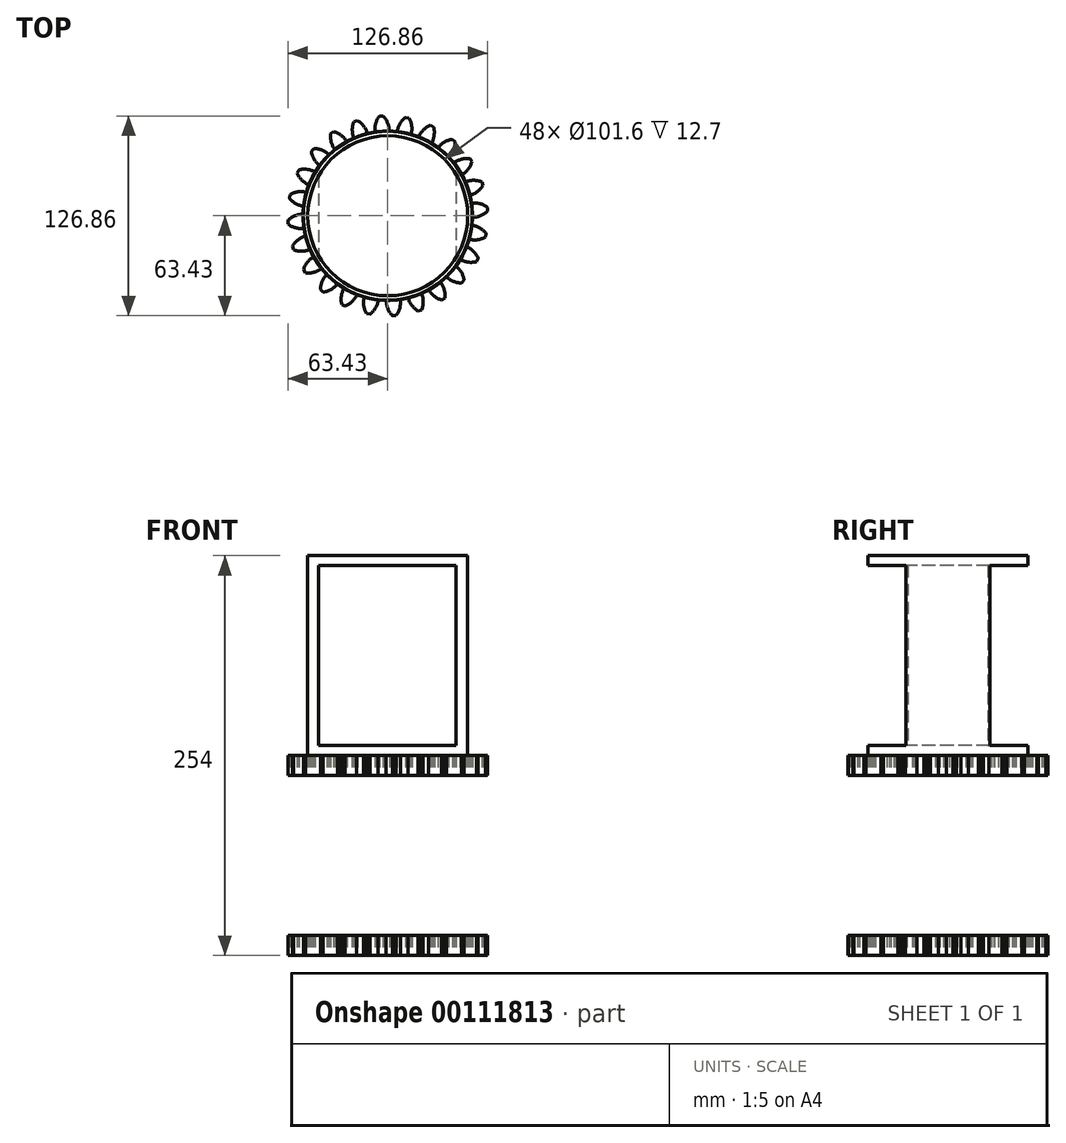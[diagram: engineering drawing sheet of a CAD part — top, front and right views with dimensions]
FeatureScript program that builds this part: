
annotation { "Feature Type Name" : "Feature", "Feature Type Description" : "" }
export const myFeature = defineFeature(function(context is Context, id is Id, definition is map)
    precondition{}
    {
        {
            var Q0;
            Q0=qCreatedBy(makeId("Top.planeOp"),FACE);
            var sketch = newSketch(context, id + "F0", { "sketchPlane" : qUnion([Q0])});
            skCircle(sketch, "E0", {"center": v(0, 0) * mm, "radius": 53.72 * mm});
            skCircle(sketch, "E1", {"center": v(0, 0) * mm, "radius": 58.67 * mm, "construction": true});
            skCircle(sketch, "E2", {"center": v(0, 0) * mm, "radius": 63.5 * mm, "construction": true});
            skLineSegment(sketch, "E3", {"start": v(0, 0) * mm, "end": v(0, 120.75) * mm, "construction": true});
            skLineSegment(sketch, "E4", {"start": v(0, 0) * mm, "end": v(-6.04, 92.19) * mm, "construction": true});
            skLineSegment(sketch, "E5", {"start": v(0, 58.67) * mm, "end": v(-93.51, 58.67) * mm, "construction": true});
            skLineSegment(sketch, "E6", {"start": v(0, 58.67) * mm, "end": v(-97.22, 23.29) * mm, "construction": true});
            skCircle(sketch, "E7", {"center": v(0, 58.67) * mm, "radius": 14.6 * mm, "construction": true});
            skCircle(sketch, "E8", {"center": v(0, 0) * mm, "radius": 55.14 * mm, "construction": true});
            skCircle(sketch, "E9", {"center": v(-13.63, 53.42) * mm, "radius": 14.6 * mm, "construction": true});
            skLineSegment(sketch, "E10", {"start": v(-2.99, 63.43) * mm, "end": v(-4.15, 63.35) * mm, "construction": true});
            skArc(sketch, "E11", {"start": v(0.97, 53.71) * mm, "mid": v(-0.03, 58.97) * mm, "end": v(-2.99, 63.43) * mm});
            skLineSegment(sketch, "E12", {"start": v(-2.99, 63.43) * mm, "end": v(-4.15, 63.35) * mm});
            skArc(sketch, "E13.MirrorCS", {"start": v(-7.98, 53.13) * mm, "mid": v(-7.66, 58.47) * mm, "end": v(-5.32, 63.28) * mm});
            skLineSegment(sketch, "E14.MirrorCS", {"start": v(-5.32, 63.28) * mm, "end": v(-4.15, 63.35) * mm, "construction": true});
            skLineSegment(sketch, "E15.MirrorCS", {"start": v(-5.32, 63.28) * mm, "end": v(-4.15, 63.35) * mm});
            skLineSegment(sketch, "E16.1.1", {"start": v(0, 0) * mm, "end": v(-7.86, 119.94) * mm, "construction": true});
            skSolve(sketch);
        }
        {
            var Q0;
            Q0 = qSketchRegion(id + "F0", true);
            extrude(context, id + "F1", {"entities" : qUnion([Q0]), "depth" : 12.7 * mm});
        }
        {
            var Q0;
            Q0=qCreatedBy(makeId("Front.planeOp"),FACE);
            var sketch = newSketch(context, id + "F2", { "sketchPlane" : qUnion([Q0])});
            skLineSegment(sketch, "E17", {"start": v(0, 0) * mm, "end": v(0, 23.47) * mm});
            skSolve(sketch);
        }
        {
            var Q0;
            Q0=makeQuery(id+"F1.opExtrude","SWEPT_BODY",BODY,{"disambiguationData":[OSD([sQuery(id+"F0.wireOp",EDGE,"E0"),sQuery(id+"F0.wireOp",EDGE,"E11"),sQuery(id+"F0.wireOp",EDGE,"E12"),sQuery(id+"F0.wireOp",EDGE,"E13.MirrorCS"),sQuery(id+"F0.wireOp",EDGE,"E15.MirrorCS")])]});
            var Q1;
            Q1=sQuery(id+"F2.wireOp",EDGE,"E17");
            circularPattern(context, id + "F3", {"entities" : qUnion([Q0]), "axis" : qUnion([Q1]), "angle" : 15 * degree, "instanceCount" : 24});
        }
        {
            var Q0;
            Q0=makeQuery(id+"F3.opPattern","COPY",FACE,{"derivedFrom":makeQuery(id+"F1.opExtrude","CAP_FACE",FACE,{"disambiguationData":[OSD([sQuery(id+"F0.wireOp",EDGE,"E0"),sQuery(id+"F0.wireOp",EDGE,"E11"),sQuery(id+"F0.wireOp",EDGE,"E12"),sQuery(id+"F0.wireOp",EDGE,"E13.MirrorCS"),sQuery(id+"F0.wireOp",EDGE,"E15.MirrorCS")])],"isStart":false}),"instanceName":"11"});
            var sketch = newSketch(context, id + "F4", { "sketchPlane" : qUnion([Q0])});
            skCircle(sketch, "E18", {"center": v(0, 0) * mm, "radius": 50.8 * mm});
            skSolve(sketch);
        }
        {
            var Q0;
            Q0 = qSketchRegion(id + "F4", true);
            extrude(context, id + "F5", {"entities" : qUnion([Q0]), "depth" : 127 * mm});
        }
        {
            var Q0;
            Q0=qCreatedBy(makeId("Front.planeOp"),FACE);
            var sketch = newSketch(context, id + "F6", { "sketchPlane" : qUnion([Q0])});
            skLineSegment(sketch, "E19.bottom", {"start": v(-43.97, 133.35) * mm, "end": v(43.26, 133.35) * mm});
            skLineSegment(sketch, "E19.top", {"start": v(-43.97, 19.05) * mm, "end": v(43.26, 19.05) * mm});
            skLineSegment(sketch, "E19.left", {"start": v(-43.97, 133.35) * mm, "end": v(-43.97, 19.05) * mm});
            skLineSegment(sketch, "E19.right", {"start": v(43.26, 133.35) * mm, "end": v(43.26, 19.05) * mm});
            skSolve(sketch);
        }
        {
            var Q0;
            Q0 = qSketchRegion(id + "F6", true);
            extrude(context, id + "F7", {"entities" : qUnion([Q0]), "operationType" : NewBodyOperationType.REMOVE, "oppositeDirection" : true, "depth" : 254 * mm});
        }
        {
            var Q0;
            Q0=makeQuery(id+"F7.boolean.opBoolean","COPY",FACE,{"derivedFrom":makeQuery(id+"F7.opExtrude","CAP_FACE",FACE,{"disambiguationData":[OSD([sQuery(id+"F6.wireOp",EDGE,"E19.bottom"),sQuery(id+"F6.wireOp",EDGE,"E19.top"),sQuery(id+"F6.wireOp",EDGE,"E19.left"),sQuery(id+"F6.wireOp",EDGE,"E19.right")])],"isStart":true})});
            var sketch = newSketch(context, id + "F8", { "sketchPlane" : qUnion([Q0])});
            skLineSegment(sketch, "E20", {"start": v(43.97, 19.05) * mm, "end": v(43.97, 133.35) * mm});
            skLineSegment(sketch, "E21", {"start": v(43.97, 133.35) * mm, "end": v(-43.26, 133.35) * mm});
            skLineSegment(sketch, "E22", {"start": v(-43.26, 133.35) * mm, "end": v(-43.26, 19.05) * mm});
            skLineSegment(sketch, "E23", {"start": v(-43.26, 19.05) * mm, "end": v(43.97, 19.05) * mm});
            skSolve(sketch);
        }
        {
            var Q0;
            Q0 = qSketchRegion(id + "F8", true);
            extrude(context, id + "F9", {"entities" : qUnion([Q0]), "operationType" : NewBodyOperationType.REMOVE, "oppositeDirection" : true, "depth" : 254 * mm});
        }
        {
            var Q0;
            Q0=makeQuery(id+"F3.opPattern","COPY",FACE,{"derivedFrom":makeQuery(id+"F1.opExtrude","CAP_FACE",FACE,{"disambiguationData":[OSD([sQuery(id+"F0.wireOp",EDGE,"E0"),sQuery(id+"F0.wireOp",EDGE,"E11"),sQuery(id+"F0.wireOp",EDGE,"E12"),sQuery(id+"F0.wireOp",EDGE,"E13.MirrorCS"),sQuery(id+"F0.wireOp",EDGE,"E15.MirrorCS")])],"isStart":true}),"instanceName":"21"});
            var sketch = newSketch(context, id + "F10", { "sketchPlane" : qUnion([Q0])});
            skCircle(sketch, "E24", {"center": v(0, 0) * mm, "radius": 50.8 * mm});
            skLineSegment(sketch, "E25", {"start": v(0, 0) * mm, "end": v(0, -521.68) * mm, "construction": true});
            skSolve(sketch);
        }
        {
            var Q0;
            Q0 = qSketchRegion(id + "F10", true);
            extrude(context, id + "F11", {"entities" : qUnion([Q0]), "operationType" : NewBodyOperationType.REMOVE, "oppositeDirection" : true, "depth" : 12.7 * mm});
        }
        {
            var Q0;
            Q0=makeQuery(id+"F1.opExtrude","SWEPT_BODY",BODY,{"disambiguationData":[OSD([sQuery(id+"F0.wireOp",EDGE,"E0"),sQuery(id+"F0.wireOp",EDGE,"E11"),sQuery(id+"F0.wireOp",EDGE,"E12"),sQuery(id+"F0.wireOp",EDGE,"E13.MirrorCS"),sQuery(id+"F0.wireOp",EDGE,"E15.MirrorCS")])]});
            var Q1;
            Q1=makeQuery(id+"F3.opPattern","COPY",BODY,{"derivedFrom":makeQuery(id+"F1.opExtrude","SWEPT_BODY",BODY,{"disambiguationData":[OSD([sQuery(id+"F0.wireOp",EDGE,"E0"),sQuery(id+"F0.wireOp",EDGE,"E11"),sQuery(id+"F0.wireOp",EDGE,"E12"),sQuery(id+"F0.wireOp",EDGE,"E13.MirrorCS"),sQuery(id+"F0.wireOp",EDGE,"E15.MirrorCS")])]}),"instanceName":"3"});
            var Q2;
            Q2=makeQuery(id+"F3.opPattern","COPY",BODY,{"derivedFrom":makeQuery(id+"F1.opExtrude","SWEPT_BODY",BODY,{"disambiguationData":[OSD([sQuery(id+"F0.wireOp",EDGE,"E0"),sQuery(id+"F0.wireOp",EDGE,"E11"),sQuery(id+"F0.wireOp",EDGE,"E12"),sQuery(id+"F0.wireOp",EDGE,"E13.MirrorCS"),sQuery(id+"F0.wireOp",EDGE,"E15.MirrorCS")])]}),"instanceName":"4"});
            var Q3;
            Q3=makeQuery(id+"F3.opPattern","COPY",BODY,{"derivedFrom":makeQuery(id+"F1.opExtrude","SWEPT_BODY",BODY,{"disambiguationData":[OSD([sQuery(id+"F0.wireOp",EDGE,"E0"),sQuery(id+"F0.wireOp",EDGE,"E11"),sQuery(id+"F0.wireOp",EDGE,"E12"),sQuery(id+"F0.wireOp",EDGE,"E13.MirrorCS"),sQuery(id+"F0.wireOp",EDGE,"E15.MirrorCS")])]}),"instanceName":"1"});
            var Q4;
            Q4=makeQuery(id+"F3.opPattern","COPY",BODY,{"derivedFrom":makeQuery(id+"F1.opExtrude","SWEPT_BODY",BODY,{"disambiguationData":[OSD([sQuery(id+"F0.wireOp",EDGE,"E0"),sQuery(id+"F0.wireOp",EDGE,"E11"),sQuery(id+"F0.wireOp",EDGE,"E12"),sQuery(id+"F0.wireOp",EDGE,"E13.MirrorCS"),sQuery(id+"F0.wireOp",EDGE,"E15.MirrorCS")])]}),"instanceName":"5"});
            var Q5;
            Q5=makeQuery(id+"F3.opPattern","COPY",BODY,{"derivedFrom":makeQuery(id+"F1.opExtrude","SWEPT_BODY",BODY,{"disambiguationData":[OSD([sQuery(id+"F0.wireOp",EDGE,"E0"),sQuery(id+"F0.wireOp",EDGE,"E11"),sQuery(id+"F0.wireOp",EDGE,"E12"),sQuery(id+"F0.wireOp",EDGE,"E13.MirrorCS"),sQuery(id+"F0.wireOp",EDGE,"E15.MirrorCS")])]}),"instanceName":"6"});
            var Q6;
            Q6=makeQuery(id+"F3.opPattern","COPY",BODY,{"derivedFrom":makeQuery(id+"F1.opExtrude","SWEPT_BODY",BODY,{"disambiguationData":[OSD([sQuery(id+"F0.wireOp",EDGE,"E0"),sQuery(id+"F0.wireOp",EDGE,"E11"),sQuery(id+"F0.wireOp",EDGE,"E12"),sQuery(id+"F0.wireOp",EDGE,"E13.MirrorCS"),sQuery(id+"F0.wireOp",EDGE,"E15.MirrorCS")])]}),"instanceName":"7"});
            var Q7;
            Q7=makeQuery(id+"F3.opPattern","COPY",BODY,{"derivedFrom":makeQuery(id+"F1.opExtrude","SWEPT_BODY",BODY,{"disambiguationData":[OSD([sQuery(id+"F0.wireOp",EDGE,"E0"),sQuery(id+"F0.wireOp",EDGE,"E11"),sQuery(id+"F0.wireOp",EDGE,"E12"),sQuery(id+"F0.wireOp",EDGE,"E13.MirrorCS"),sQuery(id+"F0.wireOp",EDGE,"E15.MirrorCS")])]}),"instanceName":"8"});
            var Q8;
            Q8=makeQuery(id+"F3.opPattern","COPY",BODY,{"derivedFrom":makeQuery(id+"F1.opExtrude","SWEPT_BODY",BODY,{"disambiguationData":[OSD([sQuery(id+"F0.wireOp",EDGE,"E0"),sQuery(id+"F0.wireOp",EDGE,"E11"),sQuery(id+"F0.wireOp",EDGE,"E12"),sQuery(id+"F0.wireOp",EDGE,"E13.MirrorCS"),sQuery(id+"F0.wireOp",EDGE,"E15.MirrorCS")])]}),"instanceName":"9"});
            var Q9;
            Q9=makeQuery(id+"F3.opPattern","COPY",BODY,{"derivedFrom":makeQuery(id+"F1.opExtrude","SWEPT_BODY",BODY,{"disambiguationData":[OSD([sQuery(id+"F0.wireOp",EDGE,"E0"),sQuery(id+"F0.wireOp",EDGE,"E11"),sQuery(id+"F0.wireOp",EDGE,"E12"),sQuery(id+"F0.wireOp",EDGE,"E13.MirrorCS"),sQuery(id+"F0.wireOp",EDGE,"E15.MirrorCS")])]}),"instanceName":"10"});
            var Q10;
            Q10=makeQuery(id+"F3.opPattern","COPY",BODY,{"derivedFrom":makeQuery(id+"F1.opExtrude","SWEPT_BODY",BODY,{"disambiguationData":[OSD([sQuery(id+"F0.wireOp",EDGE,"E0"),sQuery(id+"F0.wireOp",EDGE,"E11"),sQuery(id+"F0.wireOp",EDGE,"E12"),sQuery(id+"F0.wireOp",EDGE,"E13.MirrorCS"),sQuery(id+"F0.wireOp",EDGE,"E15.MirrorCS")])]}),"instanceName":"11"});
            var Q11;
            Q11=makeQuery(id+"F3.opPattern","COPY",BODY,{"derivedFrom":makeQuery(id+"F1.opExtrude","SWEPT_BODY",BODY,{"disambiguationData":[OSD([sQuery(id+"F0.wireOp",EDGE,"E0"),sQuery(id+"F0.wireOp",EDGE,"E11"),sQuery(id+"F0.wireOp",EDGE,"E12"),sQuery(id+"F0.wireOp",EDGE,"E13.MirrorCS"),sQuery(id+"F0.wireOp",EDGE,"E15.MirrorCS")])]}),"instanceName":"12"});
            var Q12;
            Q12=makeQuery(id+"F3.opPattern","COPY",BODY,{"derivedFrom":makeQuery(id+"F1.opExtrude","SWEPT_BODY",BODY,{"disambiguationData":[OSD([sQuery(id+"F0.wireOp",EDGE,"E0"),sQuery(id+"F0.wireOp",EDGE,"E11"),sQuery(id+"F0.wireOp",EDGE,"E12"),sQuery(id+"F0.wireOp",EDGE,"E13.MirrorCS"),sQuery(id+"F0.wireOp",EDGE,"E15.MirrorCS")])]}),"instanceName":"13"});
            var Q13;
            Q13=makeQuery(id+"F3.opPattern","COPY",BODY,{"derivedFrom":makeQuery(id+"F1.opExtrude","SWEPT_BODY",BODY,{"disambiguationData":[OSD([sQuery(id+"F0.wireOp",EDGE,"E0"),sQuery(id+"F0.wireOp",EDGE,"E11"),sQuery(id+"F0.wireOp",EDGE,"E12"),sQuery(id+"F0.wireOp",EDGE,"E13.MirrorCS"),sQuery(id+"F0.wireOp",EDGE,"E15.MirrorCS")])]}),"instanceName":"14"});
            var Q14;
            Q14=makeQuery(id+"F3.opPattern","COPY",BODY,{"derivedFrom":makeQuery(id+"F1.opExtrude","SWEPT_BODY",BODY,{"disambiguationData":[OSD([sQuery(id+"F0.wireOp",EDGE,"E0"),sQuery(id+"F0.wireOp",EDGE,"E11"),sQuery(id+"F0.wireOp",EDGE,"E12"),sQuery(id+"F0.wireOp",EDGE,"E13.MirrorCS"),sQuery(id+"F0.wireOp",EDGE,"E15.MirrorCS")])]}),"instanceName":"15"});
            var Q15;
            Q15=makeQuery(id+"F3.opPattern","COPY",BODY,{"derivedFrom":makeQuery(id+"F1.opExtrude","SWEPT_BODY",BODY,{"disambiguationData":[OSD([sQuery(id+"F0.wireOp",EDGE,"E0"),sQuery(id+"F0.wireOp",EDGE,"E11"),sQuery(id+"F0.wireOp",EDGE,"E12"),sQuery(id+"F0.wireOp",EDGE,"E13.MirrorCS"),sQuery(id+"F0.wireOp",EDGE,"E15.MirrorCS")])]}),"instanceName":"16"});
            var Q16;
            Q16=makeQuery(id+"F3.opPattern","COPY",BODY,{"derivedFrom":makeQuery(id+"F1.opExtrude","SWEPT_BODY",BODY,{"disambiguationData":[OSD([sQuery(id+"F0.wireOp",EDGE,"E0"),sQuery(id+"F0.wireOp",EDGE,"E11"),sQuery(id+"F0.wireOp",EDGE,"E12"),sQuery(id+"F0.wireOp",EDGE,"E13.MirrorCS"),sQuery(id+"F0.wireOp",EDGE,"E15.MirrorCS")])]}),"instanceName":"17"});
            var Q17;
            Q17=makeQuery(id+"F3.opPattern","COPY",BODY,{"derivedFrom":makeQuery(id+"F1.opExtrude","SWEPT_BODY",BODY,{"disambiguationData":[OSD([sQuery(id+"F0.wireOp",EDGE,"E0"),sQuery(id+"F0.wireOp",EDGE,"E11"),sQuery(id+"F0.wireOp",EDGE,"E12"),sQuery(id+"F0.wireOp",EDGE,"E13.MirrorCS"),sQuery(id+"F0.wireOp",EDGE,"E15.MirrorCS")])]}),"instanceName":"18"});
            var Q18;
            Q18=makeQuery(id+"F3.opPattern","COPY",BODY,{"derivedFrom":makeQuery(id+"F1.opExtrude","SWEPT_BODY",BODY,{"disambiguationData":[OSD([sQuery(id+"F0.wireOp",EDGE,"E0"),sQuery(id+"F0.wireOp",EDGE,"E11"),sQuery(id+"F0.wireOp",EDGE,"E12"),sQuery(id+"F0.wireOp",EDGE,"E13.MirrorCS"),sQuery(id+"F0.wireOp",EDGE,"E15.MirrorCS")])]}),"instanceName":"19"});
            var Q19;
            Q19=makeQuery(id+"F3.opPattern","COPY",BODY,{"derivedFrom":makeQuery(id+"F1.opExtrude","SWEPT_BODY",BODY,{"disambiguationData":[OSD([sQuery(id+"F0.wireOp",EDGE,"E0"),sQuery(id+"F0.wireOp",EDGE,"E11"),sQuery(id+"F0.wireOp",EDGE,"E12"),sQuery(id+"F0.wireOp",EDGE,"E13.MirrorCS"),sQuery(id+"F0.wireOp",EDGE,"E15.MirrorCS")])]}),"instanceName":"20"});
            var Q20;
            Q20=makeQuery(id+"F3.opPattern","COPY",BODY,{"derivedFrom":makeQuery(id+"F1.opExtrude","SWEPT_BODY",BODY,{"disambiguationData":[OSD([sQuery(id+"F0.wireOp",EDGE,"E0"),sQuery(id+"F0.wireOp",EDGE,"E11"),sQuery(id+"F0.wireOp",EDGE,"E12"),sQuery(id+"F0.wireOp",EDGE,"E13.MirrorCS"),sQuery(id+"F0.wireOp",EDGE,"E15.MirrorCS")])]}),"instanceName":"22"});
            var Q21;
            Q21=makeQuery(id+"F3.opPattern","COPY",BODY,{"derivedFrom":makeQuery(id+"F1.opExtrude","SWEPT_BODY",BODY,{"disambiguationData":[OSD([sQuery(id+"F0.wireOp",EDGE,"E0"),sQuery(id+"F0.wireOp",EDGE,"E11"),sQuery(id+"F0.wireOp",EDGE,"E12"),sQuery(id+"F0.wireOp",EDGE,"E13.MirrorCS"),sQuery(id+"F0.wireOp",EDGE,"E15.MirrorCS")])]}),"instanceName":"23"});
            var Q22;
            Q22=makeQuery(id+"F3.opPattern","COPY",BODY,{"derivedFrom":makeQuery(id+"F1.opExtrude","SWEPT_BODY",BODY,{"disambiguationData":[OSD([sQuery(id+"F0.wireOp",EDGE,"E0"),sQuery(id+"F0.wireOp",EDGE,"E11"),sQuery(id+"F0.wireOp",EDGE,"E12"),sQuery(id+"F0.wireOp",EDGE,"E13.MirrorCS"),sQuery(id+"F0.wireOp",EDGE,"E15.MirrorCS")])]}),"instanceName":"2"});
            var Q23;
            Q23=makeQuery(id+"F3.opPattern","COPY",BODY,{"derivedFrom":makeQuery(id+"F1.opExtrude","SWEPT_BODY",BODY,{"disambiguationData":[OSD([sQuery(id+"F0.wireOp",EDGE,"E0"),sQuery(id+"F0.wireOp",EDGE,"E11"),sQuery(id+"F0.wireOp",EDGE,"E12"),sQuery(id+"F0.wireOp",EDGE,"E13.MirrorCS"),sQuery(id+"F0.wireOp",EDGE,"E15.MirrorCS")])]}),"instanceName":"21"});
            var Q24;
            Q24=makeQuery(id+"F7.boolean.opBoolean","INTERSECT",EDGE,{"derivedFrom":[makeQuery(id+"F5.opExtrude","SWEPT_FACE",FACE,{"disambiguationData":[OSD([sQuery(id+"F4.wireOp",EDGE,"E18")])]}),makeQuery(id+"F7.opExtrude","SWEPT_FACE",FACE,{"disambiguationData":[OSD([sQuery(id+"F6.wireOp",EDGE,"E19.left")])]})]});
            transform(context, id + "F12", {"entities" : qUnion([Q0, Q1, Q2, Q3, Q4, Q5, Q6, Q7, Q8, Q9, Q10, Q11, Q12, Q13, Q14, Q15, Q16, Q17, Q18, Q19, Q20, Q21, Q22, Q23]), "transformType" : TransformType.TRANSLATION_ENTITY, "oppositeDirectionEntity" : false, "transformLine" : qUnion([Q24]), "makeCopy" : true});
        }
    });
